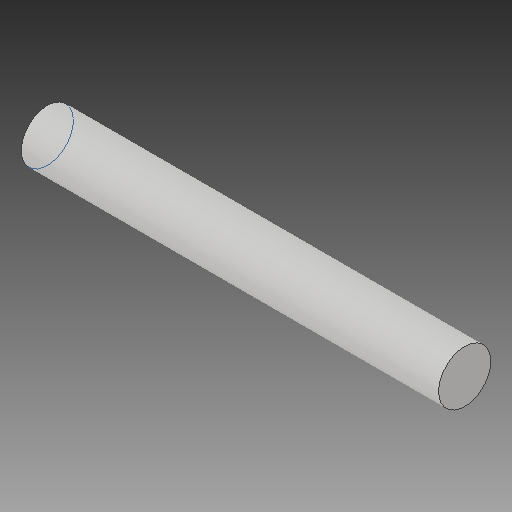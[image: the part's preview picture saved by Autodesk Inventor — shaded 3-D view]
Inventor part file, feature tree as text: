
AUTODESK INVENTOR PART (.ipt)
format: ipt  version: 2019 (Build 230136000, 136)  size: 90,624 bytes
history: native  units: in
note: dims shown in document units (in); Inventor stores cm internally (conversion verified against a paired STEP export)
features: extrude x1, sketch x1
ambient origin geometry x8: Origin, YZ Plane, XZ Plane, XY Plane, X Axis, Y Axis, Z Axis, Center Point
bodies: Solid1 (feature_tree)
feature tree (2):
  extrude  "Extrusion1"  Depth=4.0in TaperAngle=0.0deg
  sketch  "Sketch1"  dims[d0=0.5in d1=4.0in d2=0.0in]
